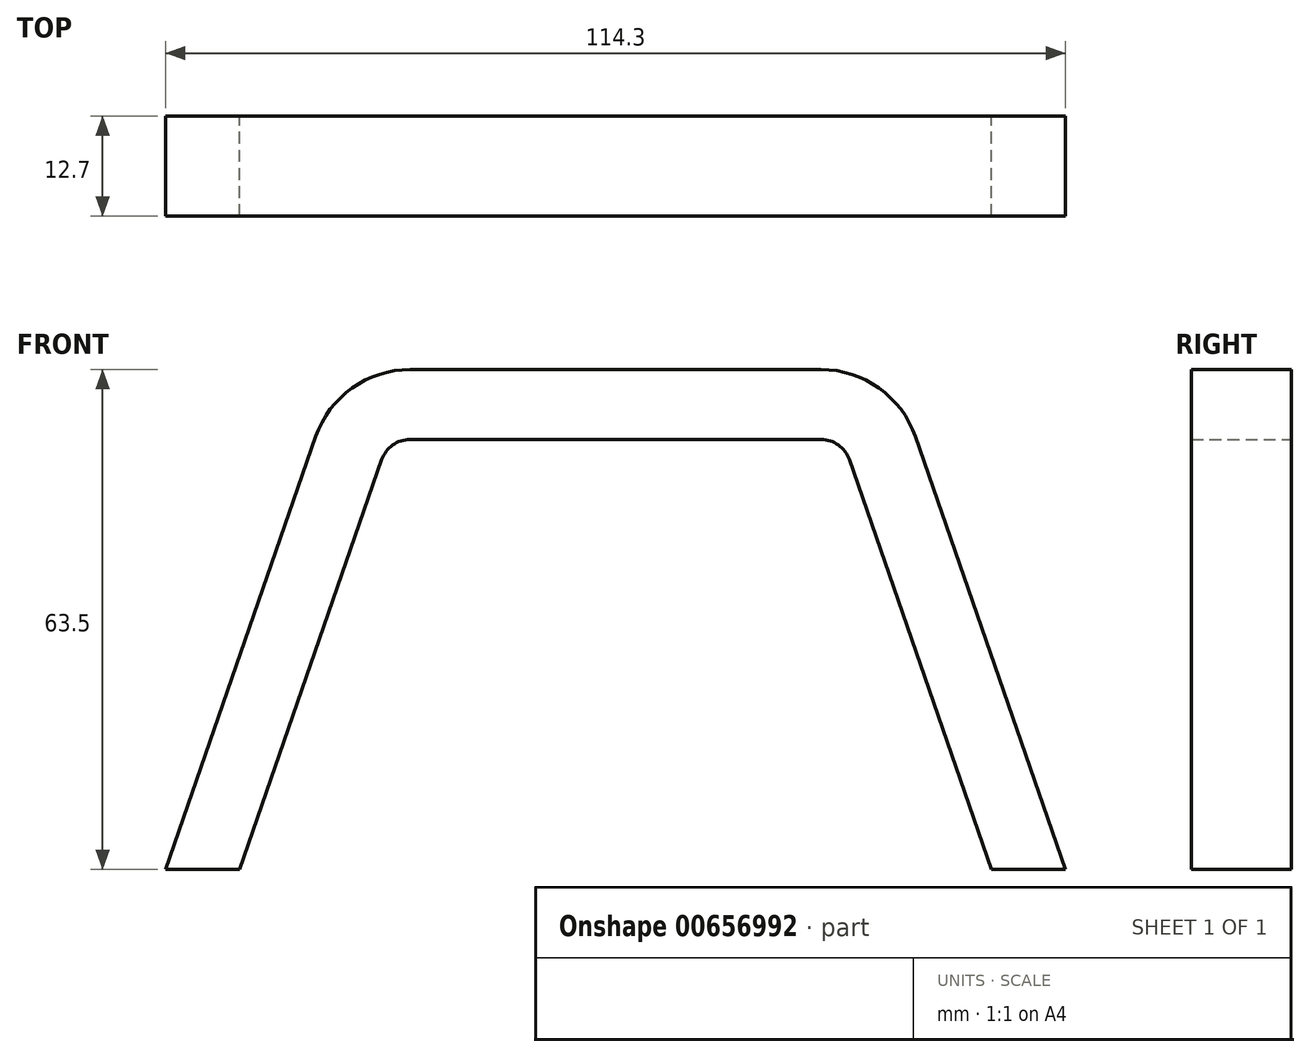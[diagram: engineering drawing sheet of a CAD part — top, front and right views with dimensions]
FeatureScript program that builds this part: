
annotation { "Feature Type Name" : "Feature", "Feature Type Description" : "" }
export const myFeature = defineFeature(function(context is Context, id is Id, definition is map)
    precondition{}
    {
        {
            var Q0;
            Q0=qCreatedBy(makeId("Front.planeOp"),FACE);
            var sketch = newSketch(context, id + "F0", { "sketchPlane" : qUnion([Q0])});
            skLineSegment(sketch, "E0", {"start": v(-81.5, -41.28) * mm, "end": v(-62.45, 13.68) * mm});
            skLineSegment(sketch, "E1", {"start": v(-81.5, -41.28) * mm, "end": v(-72.1, -41.28) * mm});
            skPoint(sketch, "E2.visualSharp", {"position": v(72.12, 0) * mm});
            skLineSegment(sketch, "E3", {"start": v(-50.46, 22.22) * mm, "end": v(1.74, 22.22) * mm});
            skLineSegment(sketch, "E4", {"start": v(13.74, 13.68) * mm, "end": v(32.8, -41.28) * mm});
            skPoint(sketch, "E5.visualSharp", {"position": v(-59.5, 22.22) * mm});
            skArc(sketch, "E5.filletArc", {"start": v(-50.46, 22.22) * mm, "mid": v(-57.82, 19.87) * mm, "end": v(-62.45, 13.68) * mm});
            skPoint(sketch, "E6.visualSharp", {"position": v(10.78, 22.22) * mm});
            skArc(sketch, "E6.filletArc", {"start": v(13.74, 13.68) * mm, "mid": v(9.1, 19.87) * mm, "end": v(1.74, 22.22) * mm});
            skLineSegment(sketch, "E7.0", {"start": v(5.34, 10.77) * mm, "end": v(23.39, -41.28) * mm});
            skLineSegment(sketch, "E7.1", {"start": v(-72.1, -41.28) * mm, "end": v(-54.06, 10.77) * mm});
            skArc(sketch, "E7.2", {"start": v(-50.46, 13.33) * mm, "mid": v(-52.66, 12.63) * mm, "end": v(-54.06, 10.77) * mm});
            skLineSegment(sketch, "E7.3", {"start": v(-50.46, 13.33) * mm, "end": v(1.74, 13.33) * mm});
            skArc(sketch, "E7.4", {"start": v(5.34, 10.77) * mm, "mid": v(3.95, 12.63) * mm, "end": v(1.74, 13.33) * mm});
            skLineSegment(sketch, "E8.trimOffspring", {"start": v(23.39, -41.28) * mm, "end": v(32.8, -41.28) * mm});
            skSolve(sketch);
        }
        {
            var Q0;
            {var subQ4=sQuery(id+"F0.wireOp",EDGE,"E0");Q0=makeQuery(id+"F0.imprint","IMPRINT",FACE,{"disambiguationData":[TD([[makeQuery(id+"F0.imprint","IMPRINT",EDGE,{"derivedFrom":subQ4}),-1.0]])]});}
            extrude(context, id + "F1", {"entities" : qUnion([Q0]), "depth" : 12.7 * mm, "offsetDistance" : 25.4 * mm});
        }
    });
